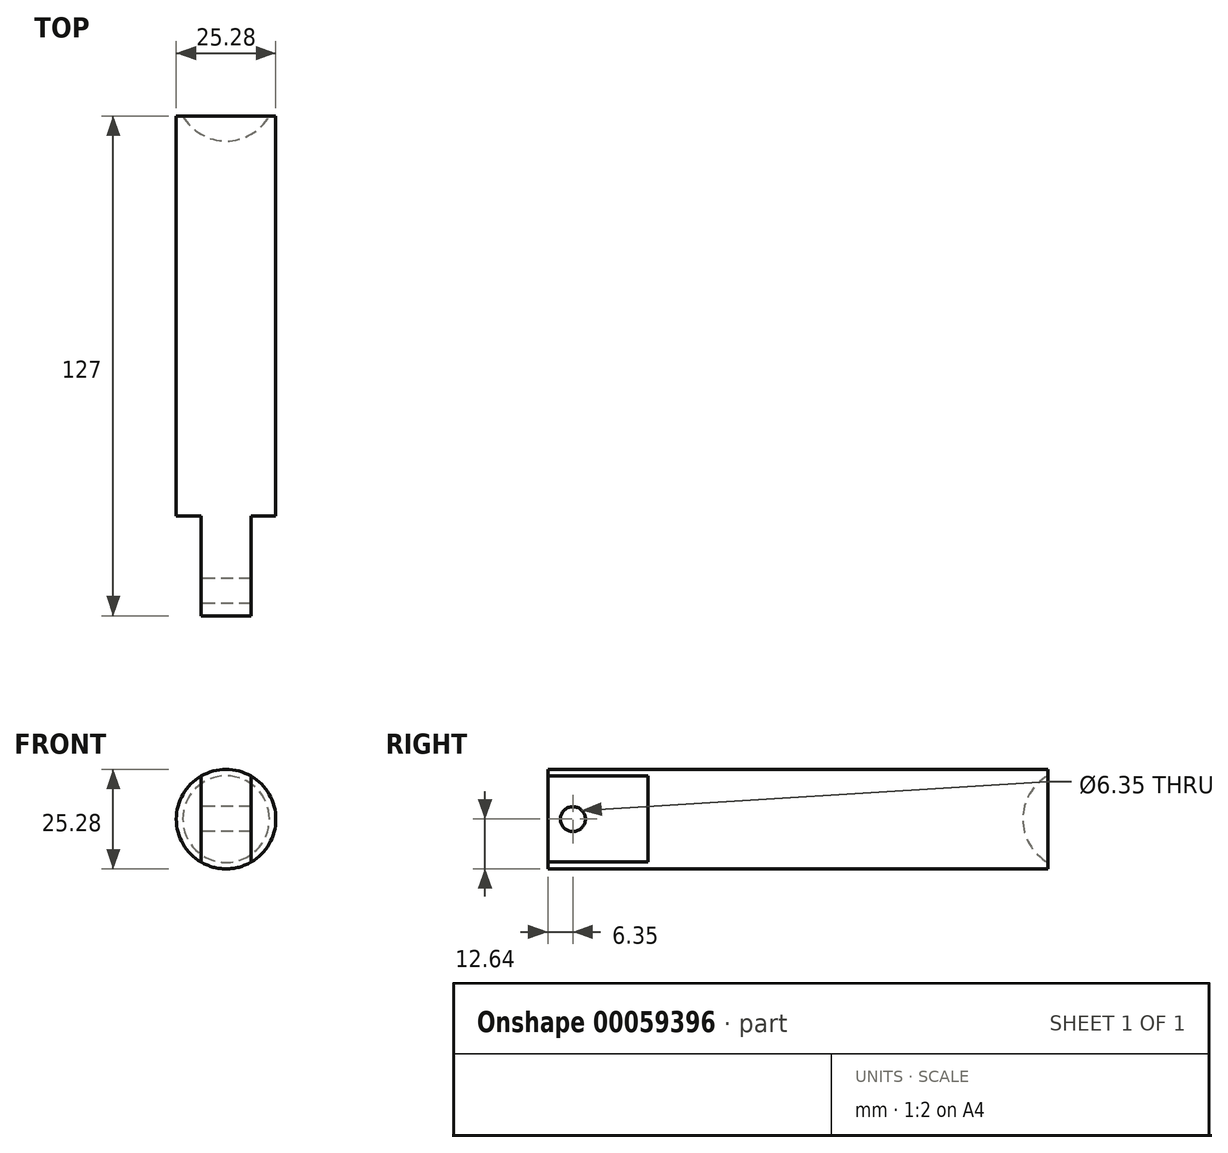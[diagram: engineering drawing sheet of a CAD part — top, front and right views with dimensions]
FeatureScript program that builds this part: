
annotation { "Feature Type Name" : "Feature", "Feature Type Description" : "" }
export const myFeature = defineFeature(function(context is Context, id is Id, definition is map)
    precondition{}
    {
        {
            var Q0;
            Q0=qCreatedBy(makeId("Front.planeOp"),FACE);
            var sketch = newSketch(context, id + "F0", { "sketchPlane" : qUnion([Q0])});
            skCircle(sketch, "E0", {"center": v(0, 0) * mm, "radius": 12.64 * mm});
            skSolve(sketch);
        }
        {
            var Q0;
            Q0 = qSketchRegion(id + "F0", true);
            extrude(context, id + "F1", {"entities" : qUnion([Q0]), "oppositeDirection" : true, "depth" : 127 * mm});
        }
        {
            var Q0;
            Q0=makeQuery(id+"F1.opExtrude","CAP_FACE",FACE,{"disambiguationData":[OSD([sQuery(id+"F0.wireOp",EDGE,"E0")])],"isStart":true});
            var sketch = newSketch(context, id + "F2", { "sketchPlane" : qUnion([Q0])});
            skLineSegment(sketch, "E1.bottom", {"start": v(-16.23, 19.05) * mm, "end": v(-6.35, 19.05) * mm});
            skLineSegment(sketch, "E1.top", {"start": v(-16.23, -22.28) * mm, "end": v(-6.35, -22.28) * mm});
            skLineSegment(sketch, "E1.left", {"start": v(-16.23, 19.05) * mm, "end": v(-16.23, -22.28) * mm});
            skLineSegment(sketch, "E1.right", {"start": v(-6.35, 19.05) * mm, "end": v(-6.35, -22.28) * mm});
            skLineSegment(sketch, "E2.bottom", {"start": v(6.35, 19.05) * mm, "end": v(19.05, 19.05) * mm});
            skLineSegment(sketch, "E2.top", {"start": v(6.35, -22.88) * mm, "end": v(19.05, -22.88) * mm});
            skLineSegment(sketch, "E2.left", {"start": v(6.35, 19.05) * mm, "end": v(6.35, -22.88) * mm});
            skLineSegment(sketch, "E2.right", {"start": v(19.05, 19.05) * mm, "end": v(19.05, -22.88) * mm});
            skSolve(sketch);
        }
        {
            var Q0;
            Q0 = qSketchRegion(id + "F2", true);
            extrude(context, id + "F3", {"entities" : qUnion([Q0]), "operationType" : NewBodyOperationType.REMOVE, "oppositeDirection" : true, "depth" : 25.4 * mm});
        }
        {
            var Q0;
            Q0=makeQuery(id+"F3.boolean.opBoolean","COPY",FACE,{"derivedFrom":makeQuery(id+"F3.opExtrude","SWEPT_FACE",FACE,{"disambiguationData":[OSD([sQuery(id+"F2.wireOp",EDGE,"E1.right")])]})});
            var sketch = newSketch(context, id + "F4", { "sketchPlane" : qUnion([Q0])});
            skCircle(sketch, "E3", {"center": v(-6.35, 0) * mm, "radius": 3.18 * mm});
            skPoint(sketch, "E3.centerSnap0", {"position": v(0, 0) * mm});
            skSolve(sketch);
        }
        {
            var Q0;
            Q0 = qSketchRegion(id + "F4", true);
            extrude(context, id + "F5", {"entities" : qUnion([Q0]), "operationType" : NewBodyOperationType.REMOVE, "oppositeDirection" : true, "depth" : 25.4 * mm});
        }
        {
            var Q0;
            Q0=qCreatedBy(makeId("Front.planeOp"),FACE);
            cPlane(context, id + "F6", {"entities" : qUnion([Q0]), "cplaneType" : CPlaneType.OFFSET, "offset" : 133.35 * mm, "oppositeDirection" : true, "width" : 152.4 * mm, "height" : 152.4 * mm});
        }
        {
            var Q0;
            Q0=qCreatedBy(id+"F6.planeOp",FACE);
            var sketch = newSketch(context, id + "F7", { "sketchPlane" : qUnion([Q0])});
            skLineSegment(sketch, "E4", {"start": v(16.91, 0) * mm, "end": v(-13.65, 0) * mm, "construction": true});
            skArc(sketch, "E5", {"start": v(12.7, 0) * mm, "mid": v(0, 12.7) * mm, "end": v(-12.7, 0) * mm});
            skLineSegment(sketch, "E6", {"start": v(12.7, 0) * mm, "end": v(-12.7, 0) * mm});
            skSolve(sketch);
        }
        {
            var Q0;
            Q0 = qSketchRegion(id + "F7", true);
            var Q1;
            Q1=sQuery(id+"F7.wireOp",EDGE,"E4");
            revolve(context, id + "F8", {"operationType" : NewBodyOperationType.REMOVE, "entities" : qUnion([Q0]), "axis" : qUnion([Q1]), "revolveType" : RevolveType.FULL, "oppositeDirection" : true});
        }
    });
